# Revit family: Electrical_Switchgear_Modelec_Confidence-Collection-long-narrow_FRA888
name_source: partatom
category: Installations électriques
units: mm (PartAtom-declared; Revit-internal decimal feet)

## family parameters
Conserver l'orientation des annotations = Non
Cote de connecteur circulaire = Utiliser le diamètre
Couper avec des vides une fois chargée = Non
Hôte = Face
Numéro OmniClass = 23.80.50.11.14
Partagée = Non
Repere pour localisation dans la piece = Non
Titre OmniClass = Switches
Type d'élément = Normal

## types (1)
- Par défaut - veuillez charger le catalogue des types de familles Revit
    Apparent Load = 0 VA
    B1 = Oui
    B1 + LED = Non
    B1 + LED Loin = Non
    B1 + P1 Loin = Non
    B2 = Non
    B2 Loin = Non
    B3 = Non
    Bouton Centre = Non
    Boutons de Région de Masquage Visibles = Non
    Boutons du Milieu = Non
    Derniers Boutons = Non
    Description = Les interrupteurs de confiance sur des plaques longues et étroites sont à la fois discrets et élégants. Les plaques sont en laiton, fabriquées en France, et offrent une large gamme de fonctions (boutons poussoirs et bascules dans 4 finitions, avec ou sans LED). La collection Confiance est un grand classique du monde de la décoration. Ses formes épurées et le détail de ses finitions soignées en font un incontournable pour vos projets résidentiels, hôteliers ou tertiaires. La collection Confiance mérite son nom. La bonne touche, quel que soit votre choix esthétique. Disponible en 12 finitions.
    Description du Connecteur = Interrupteur
    Elévation par défaut = 0 mm  [stored 0 ft]
    Fabricant = Modelec
    Installation instructions = https://www.modelec.com
    LED Loin = Non
    LED Visible = Non
    Levier Bas = Non
    Levier Centre = Oui
    Levier Haut = Non
    Leviers de Haut et de Bas = 25 mm  [stored 0.082021 ft]
    Leviers de Région de Masquage Visibles = Oui
    Modèle = Confidence Collection
    Number of Poles = 1
    P1 = Non
    P1 + LED Loin = Non
    P1 Loin = Non
    P2 = Non
    P2  Loin = Non
    P3 = Non
    P4 = Non
    P5 = Non
    Power Factor = 1
    Product Documentation Link = https://www.modelec.com
    Product Page URL = https://www.modelec.com
    Product data url = https://bimobject.com
    URL = https://www.modelec.com
    Version = 1
    Vides de Haut et de Bas = 22 mm  [stored 0.0721785 ft]
    Voltage = 220 V
    Weight - Mass = 0.12 kg

note: [stored X ft] marks values corroborated as IEEE doubles in the binary element streams (Revit-internal decimal feet)

## geometry (parser evidence)
native form markers: Sweep x3
no freeform markers — native parametric forms only
